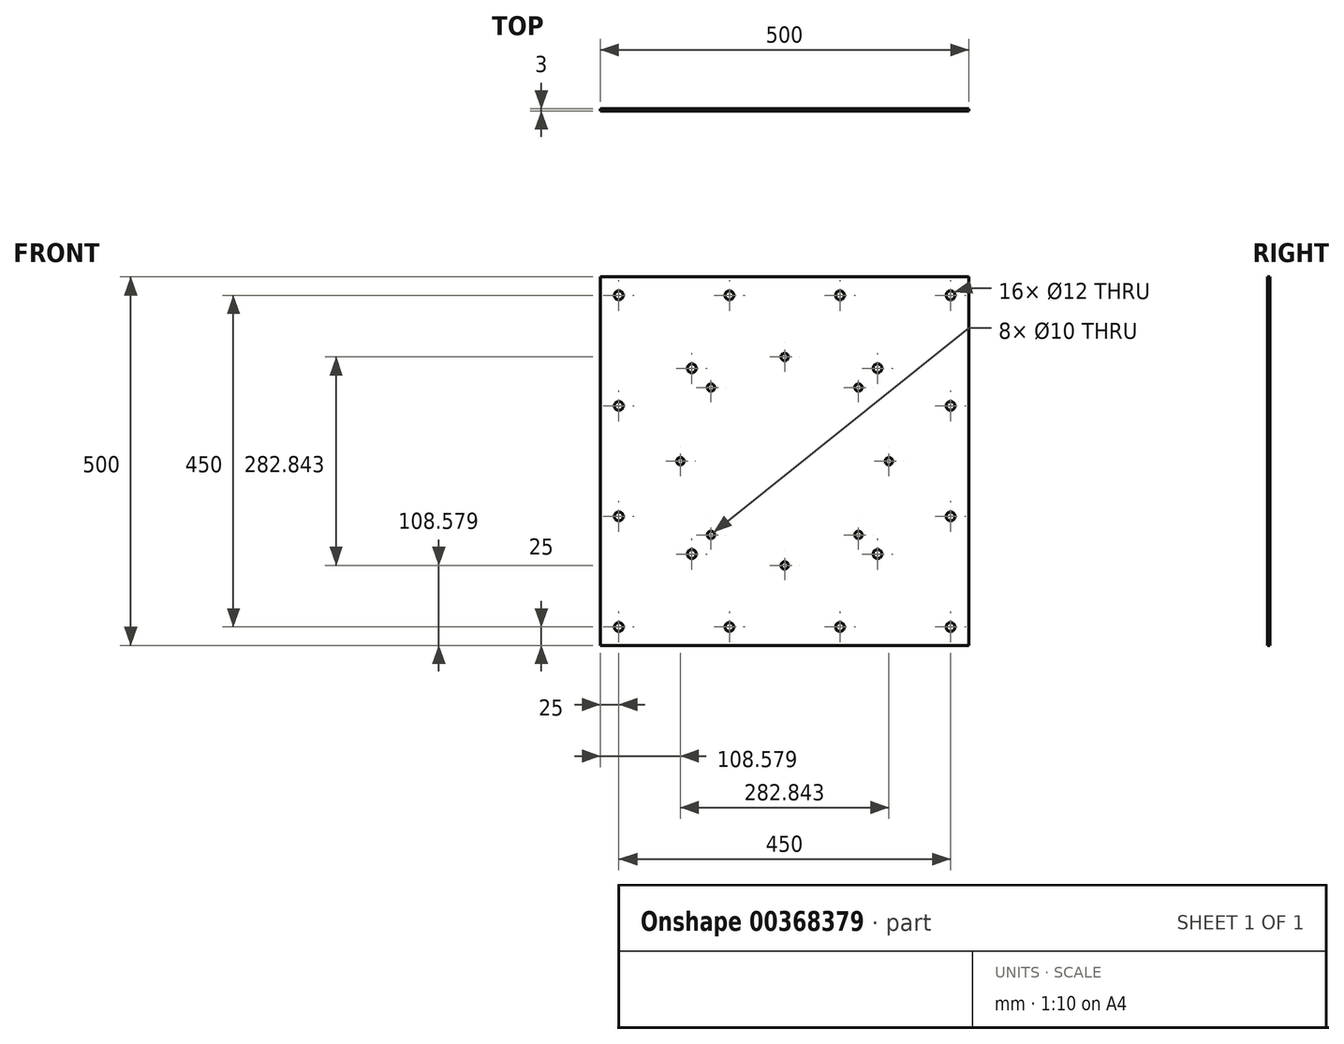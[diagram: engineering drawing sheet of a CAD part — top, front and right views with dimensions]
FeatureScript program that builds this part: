
annotation { "Feature Type Name" : "Feature", "Feature Type Description" : "" }
export const myFeature = defineFeature(function(context is Context, id is Id, definition is map)
    precondition{}
    {
        {
            var Q0;
            Q0=qCreatedBy(makeId("Front.planeOp"),FACE);
            var sketch = newSketch(context, id + "F0", { "sketchPlane" : qUnion([Q0])});
            skLineSegment(sketch, "E0.bottom", {"start": v(0, 0) * mm, "end": v(500, 0) * mm});
            skLineSegment(sketch, "E0.top", {"start": v(0, 500) * mm, "end": v(500, 500) * mm});
            skLineSegment(sketch, "E0.left", {"start": v(0, 0) * mm, "end": v(0, 500) * mm});
            skLineSegment(sketch, "E0.right", {"start": v(500, 0) * mm, "end": v(500, 500) * mm});
            skSolve(sketch);
        }
        {
            var Q0;
            Q0 = qSketchRegion(id + "F0", true);
            extrude(context, id + "F1", {"entities" : qUnion([Q0]), "depth" : 3 * mm});
        }
        {
            var Q0;
            Q0=makeQuery(id+"F1.opExtrude","CAP_FACE",FACE,{"disambiguationData":[OSD([sQuery(id+"F0.wireOp",EDGE,"E0.bottom"),sQuery(id+"F0.wireOp",EDGE,"E0.top"),sQuery(id+"F0.wireOp",EDGE,"E0.left"),sQuery(id+"F0.wireOp",EDGE,"E0.right")])],"isStart":false});
            var sketch = newSketch(context, id + "F2", { "sketchPlane" : qUnion([Q0])});
            skLineSegment(sketch, "E1.bottom", {"start": v(150, 350) * mm, "end": v(350, 350) * mm});
            skLineSegment(sketch, "E1.top", {"start": v(150, 150) * mm, "end": v(350, 150) * mm});
            skLineSegment(sketch, "E1.left", {"start": v(150, 350) * mm, "end": v(150, 150) * mm});
            skLineSegment(sketch, "E1.right", {"start": v(350, 350) * mm, "end": v(350, 150) * mm});
            skLineSegment(sketch, "E2.1.0", {"start": v(108.58, 250) * mm, "end": v(250, 108.58) * mm});
            skLineSegment(sketch, "E2.1.1", {"start": v(250, 391.42) * mm, "end": v(391.42, 250) * mm});
            skLineSegment(sketch, "E2.1.2", {"start": v(250, 391.42) * mm, "end": v(108.58, 250) * mm});
            skLineSegment(sketch, "E2.1.3", {"start": v(391.42, 250) * mm, "end": v(250, 108.58) * mm});
            skPoint(sketch, "E2.center", {"position": v(250, 250) * mm});
            skLineSegment(sketch, "E2.anchor1", {"start": v(250, 250) * mm, "end": v(150, 150) * mm, "construction": true});
            skLineSegment(sketch, "E2.anchor2", {"start": v(250, 250) * mm, "end": v(108.58, 250) * mm, "construction": true});
            skLineSegment(sketch, "E3", {"start": v(0, 0) * mm, "end": v(500, 500) * mm});
            skLineSegment(sketch, "E4", {"start": v(0, 500) * mm, "end": v(500, 0) * mm});
            skSolve(sketch);
        }
        {
            var Q0;
            Q0=sQuery(id+"F2.wireOp",VERTEX,"E1.bottom.start");
            var Q1;
            Q1=sQuery(id+"F2.wireOp",VERTEX,"E2.1.2.start");
            var Q2;
            Q2=sQuery(id+"F2.wireOp",VERTEX,"E1.right.start");
            var Q3;
            Q3=sQuery(id+"F2.wireOp",VERTEX,"E2.1.3.start");
            var Q4;
            Q4=sQuery(id+"F2.wireOp",VERTEX,"E1.right.end");
            var Q5;
            Q5=sQuery(id+"F2.wireOp",VERTEX,"E2.1.3.end");
            var Q6;
            Q6=sQuery(id+"F2.wireOp",VERTEX,"E2.anchor1.end");
            var Q7;
            Q7=sQuery(id+"F2.wireOp",VERTEX,"E2.1.2.end");
            var Q8;
            Q8=makeQuery(id+"F1.opExtrude","SWEPT_BODY",BODY,{"disambiguationData":[OSD([sQuery(id+"F0.wireOp",EDGE,"E0.bottom"),sQuery(id+"F0.wireOp",EDGE,"E0.top"),sQuery(id+"F0.wireOp",EDGE,"E0.left"),sQuery(id+"F0.wireOp",EDGE,"E0.right")])]});
            hole(context, id + "F3", {"style" : HoleStyle.SIMPLE, "endStyle" : HoleEndStyle.THROUGH, "holeDiameter" : 10 * mm, "isTappedThrough" : true, "tappedDepth" : 12 * mm, "tapClearance" : 3, "locations" : qUnion([Q0, Q1, Q2, Q3, Q4, Q5, Q6, Q7]), "scope" : qUnion([Q8])});
        }
        {
            var Q0;
            Q0=makeQuery(id+"F1.opExtrude","CAP_FACE",FACE,{"disambiguationData":[OSD([sQuery(id+"F0.wireOp",EDGE,"E0.bottom"),sQuery(id+"F0.wireOp",EDGE,"E0.top"),sQuery(id+"F0.wireOp",EDGE,"E0.left"),sQuery(id+"F0.wireOp",EDGE,"E0.right")])],"isStart":false});
            var sketch = newSketch(context, id + "F4", { "sketchPlane" : qUnion([Q0])});
            skLineSegment(sketch, "E5.bottom", {"start": v(25, 475) * mm, "end": v(475, 475) * mm, "construction": true});
            skLineSegment(sketch, "E5.top", {"start": v(25, 25) * mm, "end": v(475, 25) * mm, "construction": true});
            skLineSegment(sketch, "E5.left", {"start": v(25, 475) * mm, "end": v(25, 25) * mm, "construction": true});
            skLineSegment(sketch, "E5.right", {"start": v(475, 475) * mm, "end": v(475, 25) * mm, "construction": true});
            skPoint(sketch, "E6", {"position": v(25, 325) * mm});
            skPoint(sketch, "E7", {"position": v(25, 175) * mm});
            skPoint(sketch, "E8", {"position": v(175, 25) * mm});
            skPoint(sketch, "E9", {"position": v(325, 25) * mm});
            skPoint(sketch, "E10", {"position": v(475, 175) * mm});
            skPoint(sketch, "E11", {"position": v(475, 325) * mm});
            skPoint(sketch, "E12", {"position": v(325, 475) * mm});
            skPoint(sketch, "E13", {"position": v(175, 475) * mm});
            skSolve(sketch);
        }
        {
            var Q0;
            Q0=sQuery(id+"F4.wireOp",VERTEX,"E6");
            var Q1;
            Q1=sQuery(id+"F4.wireOp",VERTEX,"E5.left.start");
            var Q2;
            Q2=sQuery(id+"F4.wireOp",VERTEX,"E13");
            var Q3;
            Q3=sQuery(id+"F4.wireOp",VERTEX,"E12");
            var Q4;
            Q4=sQuery(id+"F4.wireOp",VERTEX,"E5.right.start");
            var Q5;
            Q5=sQuery(id+"F4.wireOp",VERTEX,"E11");
            var Q6;
            Q6=sQuery(id+"F4.wireOp",VERTEX,"E10");
            var Q7;
            Q7=sQuery(id+"F4.wireOp",VERTEX,"E5.right.end");
            var Q8;
            Q8=sQuery(id+"F4.wireOp",VERTEX,"E9");
            var Q9;
            Q9=sQuery(id+"F4.wireOp",VERTEX,"E8");
            var Q10;
            Q10=sQuery(id+"F4.wireOp",VERTEX,"E5.left.end");
            var Q11;
            Q11=sQuery(id+"F4.wireOp",VERTEX,"E7");
            var Q12;
            Q12=makeQuery(id+"F1.opExtrude","SWEPT_BODY",BODY,{"disambiguationData":[OSD([sQuery(id+"F0.wireOp",EDGE,"E0.bottom"),sQuery(id+"F0.wireOp",EDGE,"E0.top"),sQuery(id+"F0.wireOp",EDGE,"E0.left"),sQuery(id+"F0.wireOp",EDGE,"E0.right")])]});
            hole(context, id + "F5", {"style" : HoleStyle.SIMPLE, "endStyle" : HoleEndStyle.THROUGH, "holeDiameter" : 12 * mm, "isTappedThrough" : true, "tappedDepth" : 12 * mm, "tapClearance" : 3, "locations" : qUnion([Q0, Q1, Q2, Q3, Q4, Q5, Q6, Q7, Q8, Q9, Q10, Q11]), "scope" : qUnion([Q12])});
        }
        {
            var Q0;
            Q0=makeQuery(id+"F1.opExtrude","CAP_FACE",FACE,{"disambiguationData":[OSD([sQuery(id+"F0.wireOp",EDGE,"E0.bottom"),sQuery(id+"F0.wireOp",EDGE,"E0.top"),sQuery(id+"F0.wireOp",EDGE,"E0.left"),sQuery(id+"F0.wireOp",EDGE,"E0.right")])],"isStart":false});
            var sketch = newSketch(context, id + "F6", { "sketchPlane" : qUnion([Q0])});
            skLineSegment(sketch, "E14.bottom", {"start": v(124, 376) * mm, "end": v(376, 376) * mm, "construction": true});
            skLineSegment(sketch, "E14.top", {"start": v(124, 124) * mm, "end": v(376, 124) * mm, "construction": true});
            skLineSegment(sketch, "E14.left", {"start": v(124, 376) * mm, "end": v(124, 124) * mm, "construction": true});
            skLineSegment(sketch, "E14.right", {"start": v(376, 376) * mm, "end": v(376, 124) * mm, "construction": true});
            skLineSegment(sketch, "E15", {"start": v(0, 500) * mm, "end": v(500, 0) * mm, "construction": true});
            skLineSegment(sketch, "E16", {"start": v(0, 0) * mm, "end": v(500, 500) * mm, "construction": true});
            skSolve(sketch);
        }
        {
            var Q0;
            Q0=sQuery(id+"F6.wireOp",VERTEX,"E14.left.start");
            var Q1;
            Q1=sQuery(id+"F6.wireOp",VERTEX,"E14.right.start");
            var Q2;
            Q2=sQuery(id+"F6.wireOp",VERTEX,"E14.right.end");
            var Q3;
            Q3=sQuery(id+"F6.wireOp",VERTEX,"E14.left.end");
            var Q4;
            Q4=makeQuery(id+"F1.opExtrude","SWEPT_BODY",BODY,{"disambiguationData":[OSD([sQuery(id+"F0.wireOp",EDGE,"E0.bottom"),sQuery(id+"F0.wireOp",EDGE,"E0.top"),sQuery(id+"F0.wireOp",EDGE,"E0.left"),sQuery(id+"F0.wireOp",EDGE,"E0.right")])]});
            hole(context, id + "F7", {"style" : HoleStyle.SIMPLE, "endStyle" : HoleEndStyle.THROUGH, "holeDiameter" : 12 * mm, "isTappedThrough" : true, "tappedDepth" : 12 * mm, "tapClearance" : 3, "locations" : qUnion([Q0, Q1, Q2, Q3]), "scope" : qUnion([Q4])});
        }
    });
